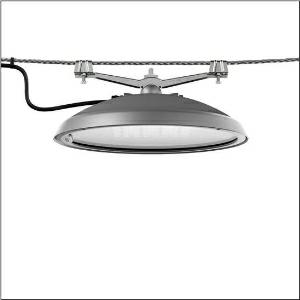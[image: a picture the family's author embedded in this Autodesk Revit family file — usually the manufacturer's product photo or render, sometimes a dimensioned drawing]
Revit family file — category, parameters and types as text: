
# Revit family: dl_50_iq_mini___st1_0s_5xa248w41f08ge_1ff8
name_source: partatom
category: Lighting Fixtures
units: mm (PartAtom-declared; Revit-internal decimal feet)

## family parameters
Cut with Voids When Loaded = No
Host = Face
Light Source = No
Part Type = Normal
Room Calculation Point = No
Round Connector Dimension = Use Diameter
Shared = No

## types (1)
- --- (1 x LED, 5190 lm, 31.2 W, 4000K)
    Apparent Load = 31 VA
    CIE Flux Codes = 37 72 97 100 100
    Color Rendering = 70
    Color Temperature = 4000K
    Default Elevation = 1800 mm
    Description = DL 50 iQ mini, catenary luminaire, primary light control with lens, of PMMA, primary optical cover: cover, of toughened safety glass, transparent, light distribution: ST1.0s, light emission: direct distribution, primary light characteristic: symmetric, installation type: suspended mounting, LED, High Power LED, rated luminous flux: 5.190lm, luminous efficacy: 166lm/W, light colour: 740, colour temperature: 4000K, control gear: iQ Street-Remote, control: optimised constant luminous flux control (CLO 2.0), Desk-Remote (wireless, voltage-free reading and setting of iQ features in the workshop via application-optimized NFC function/RFID function), Light-Fading, Smart-Wire, Night-Set, Lumen-Switch, Temp-Guard, Auto-Match, Street-Remote, mains connection: 230..240V, AC, 50/60Hz, start of lifetime: 31W, end of service life: 32W, reduction: 15W, luminaire housing, of diecast aluminium, powder-coated, SITECO metallic grey (DB 702S), diameter: 500mm, height: 115mm, mounting height: 4..12m, protection rating (complete): IP66, insulation class (complete): insulation class II (safety insulation), certification: CE, ENEC, ENEC+, VDE, impact resistance: IK08, permissible operating ambient temperature for outdoor applications: -25..+40°C, standard-compliant lighting for roads and squares, packaging unit: 1 piece

Light Distribution: ST1.0s
    Height = 124 mm  [stored 0.406824 ft]
    Lamp = 1 x LED
    Lamp Light Flux = 5190 lm
    Lamp Power = 31.2 W
    Lamp count = 1
    Length = 500 mm
    Luminous efficacy = 166 lm/W
    Manufacturer = Siteco
    ModVariant = No
    Model = 5XA248W41F08GE
    Number of Poles = 1
    OnlyDefault = Yes
    Power Factor = 1
    Product Name = DL 50 iQ mini | ST1.0s
    Product group = catenary luminaire
    ProductGroupID = 6300
    Protection Class = Protection class II
    Protection Degree = IP 66
    RLX_Detail_Level = 1
    RLX_Emergency_Light_Flux = 0 lm
    RLX_Emergency_Type = 0
    RLX_Emergency_Type_DB = No
    RlxData = <blob elided: 124377 chars, md5=c487eec9>
    Socket = socket
    Standby Power = 0 W
    System Light Flux = 5190 lm
    System Power = 31 W
    Type Comments = factory setting: luminous flux: 100 % | dim-lin: 254 | 325 mA
    Type Image = l_1242791.jpg
    URL = http://relux.com
    VarID = @adj_140325
    Voltage = 0 V
    Weight = 0.00 kg
    Width = 0 mm  [stored 0 ft]

note: [stored X ft] marks values corroborated as IEEE doubles in the binary element streams (Revit-internal decimal feet)

## geometry (parser evidence)
native form markers: Blend x4, Sweep x12
no freeform markers — native parametric forms only
